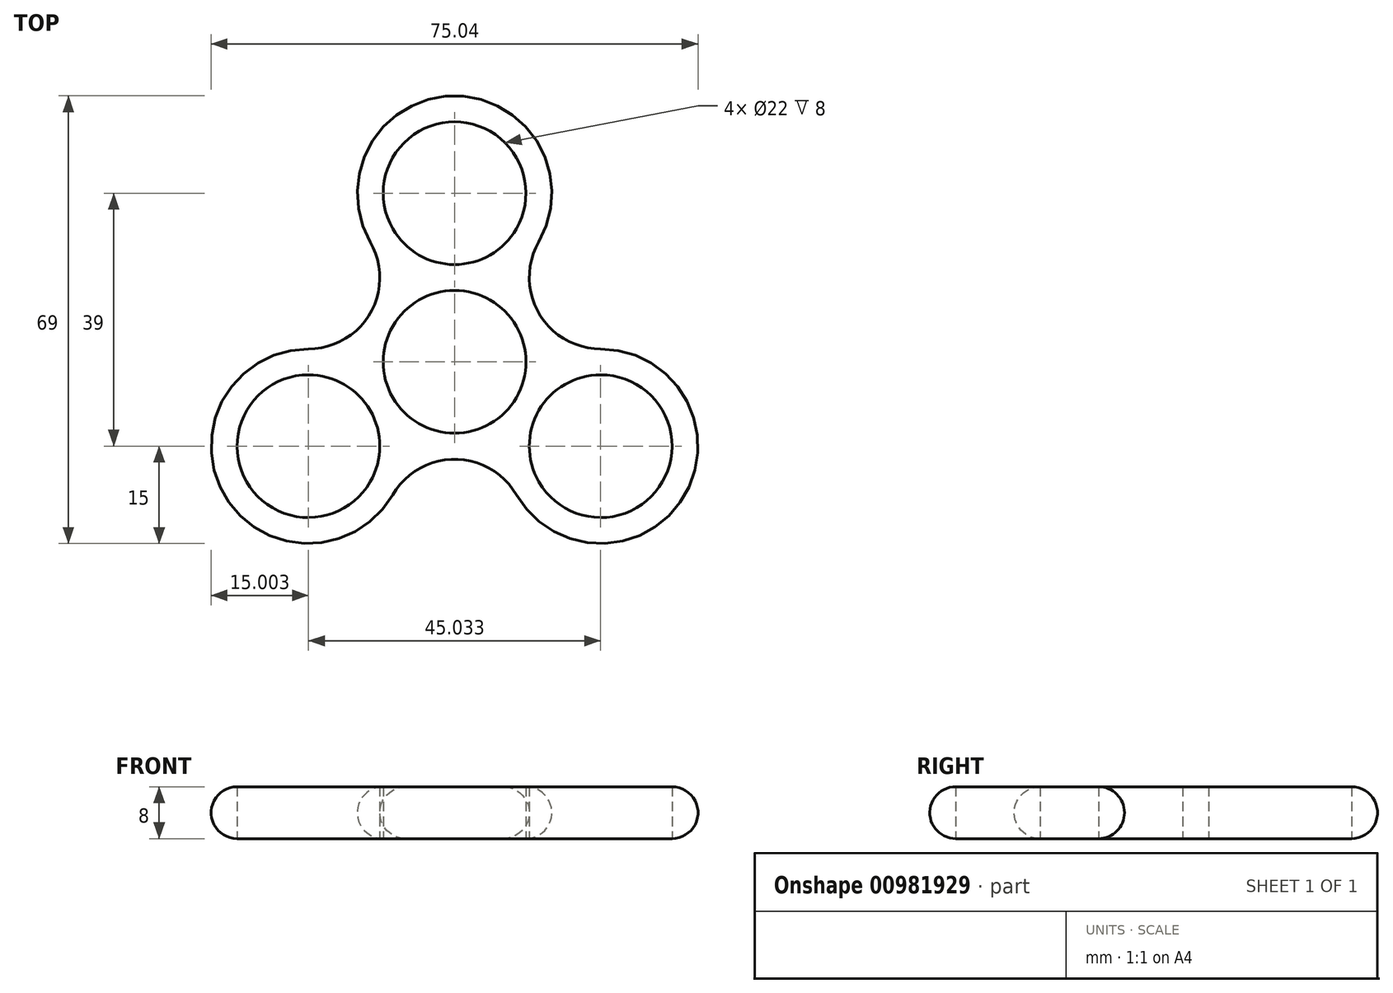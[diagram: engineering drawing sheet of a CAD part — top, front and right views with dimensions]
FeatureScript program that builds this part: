
annotation { "Feature Type Name" : "Feature", "Feature Type Description" : "" }
export const myFeature = defineFeature(function(context is Context, id is Id, definition is map)
    precondition{}
    {
        {
            var Q0;
            Q0=qCreatedBy(makeId("Top.planeOp"),FACE);
            var sketch = newSketch(context, id + "F0", { "sketchPlane" : qUnion([Q0])});
            skCircle(sketch, "E0", {"center": v(0, 0) * mm, "radius": 11 * mm});
            skCircle(sketch, "E1", {"center": v(0, 26) * mm, "radius": 11 * mm});
            skArc(sketch, "E2", {"start": v(13, 18.5) * mm, "mid": v(0, 41) * mm, "end": v(-13, 18.5) * mm});
            skArc(sketch, "E3.1.0", {"start": v(-22.52, 2) * mm, "mid": v(-35.5, -20.5) * mm, "end": v(-9.53, -20.5) * mm});
            skCircle(sketch, "E3.1.1", {"center": v(-22.52, -13) * mm, "radius": 11 * mm});
            skArc(sketch, "E3.2.0", {"start": v(15.02, 0) * mm, "mid": v(15, -0.01) * mm, "end": v(15, -0.02) * mm});
            skCircle(sketch, "E3.2.1", {"center": v(22.52, -13) * mm, "radius": 11 * mm});
            skArc(sketch, "E4", {"start": v(7.52, 12.98) * mm, "mid": v(7.5, 13) * mm, "end": v(7.48, 13) * mm});
            skLineSegment(sketch, "E5", {"start": v(7.52, -13) * mm, "end": v(7.48, -13) * mm, "construction": true});
            skArc(sketch, "E6", {"start": v(-22.52, 2) * mm, "mid": v(-13, 7.5) * mm, "end": v(-13, 18.5) * mm});
            skArc(sketch, "E7.1.0", {"start": v(9.53, -20.5) * mm, "mid": v(0, -15) * mm, "end": v(-9.53, -20.5) * mm});
            skArc(sketch, "E7.2.0", {"start": v(13, 18.5) * mm, "mid": v(13, 7.5) * mm, "end": v(22.52, 2) * mm});
            skLineSegment(sketch, "E8.trimOffspring", {"start": v(7.52, 12.98) * mm, "end": v(7.5, 13) * mm, "construction": true});
            skArc(sketch, "E9.trimOffspring", {"start": v(-7.48, 13) * mm, "mid": v(-7.5, 13) * mm, "end": v(-7.52, 12.98) * mm});
            skArc(sketch, "E10.trimOffspring", {"start": v(7.48, 13) * mm, "mid": v(7.5, 13) * mm, "end": v(7.5, 13) * mm});
            skArc(sketch, "E11.trimOffspring", {"start": v(-7.5, 13) * mm, "mid": v(-7.5, 13) * mm, "end": v(-7.48, 13) * mm});
            skArc(sketch, "E12.trimOffspring", {"start": v(-15, 0.02) * mm, "mid": v(-15, 0) * mm, "end": v(-15, -0.02) * mm});
            skLineSegment(sketch, "E13.trimOffspring", {"start": v(-7.52, 12.98) * mm, "end": v(-7.5, 13) * mm, "construction": true});
            skLineSegment(sketch, "E14.trimOffspring", {"start": v(-15.02, 0) * mm, "end": v(-15, 0.02) * mm, "construction": true});
            skArc(sketch, "E15.trimOffspring", {"start": v(-7.52, -12.98) * mm, "mid": v(-7.5, -13) * mm, "end": v(-7.48, -13) * mm});
            skArc(sketch, "E16.trimOffspring", {"start": v(-15, -0.02) * mm, "mid": v(-15, -0.01) * mm, "end": v(-15.02, 0) * mm});
            skArc(sketch, "E17.trimOffspring", {"start": v(7.52, -12.98) * mm, "mid": v(7.52, -13) * mm, "end": v(7.52, -13) * mm});
            skArc(sketch, "E18.trimOffspring", {"start": v(15, -0.02) * mm, "mid": v(15, 0) * mm, "end": v(15, 0.02) * mm});
            skLineSegment(sketch, "E19.trimOffspring", {"start": v(15.02, 0) * mm, "end": v(15, 0.02) * mm, "construction": true});
            skArc(sketch, "E20.trimOffspring", {"start": v(7.48, -13) * mm, "mid": v(7.5, -13) * mm, "end": v(7.52, -12.98) * mm});
            skArc(sketch, "E21.trimOffspring", {"start": v(9.53, -20.5) * mm, "mid": v(35.5, -20.5) * mm, "end": v(22.52, 2) * mm});
            skLineSegment(sketch, "E22.trimOffspring", {"start": v(-7.48, -13) * mm, "end": v(-7.52, -13) * mm, "construction": true});
            skArc(sketch, "E23.trimOffspring", {"start": v(-7.52, -13) * mm, "mid": v(-7.52, -13) * mm, "end": v(-7.52, -12.98) * mm});
            skSolve(sketch);
        }
        {
            var Q0;
            Q0=makeQuery(id+"F0.imprint","IMPRINT",FACE,{"disambiguationData":[TD([[makeQuery(id+"F0.imprint","IMPRINT",EDGE,{"derivedFrom":sQuery(id+"F0.wireOp",EDGE,"E0")}),-1.0]])]});
            extrude(context, id + "F1", {"entities" : qUnion([Q0]), "depth" : 8 * mm, "offsetDistance" : 25 * mm});
        }
        {
            var Q0;
            Q0=makeQuery(id+"F1.opExtrude","SWEPT_FACE",FACE,{"disambiguationData":[OSD([sQuery(id+"F0.wireOp",EDGE,"E21.trimOffspring")])]});
            var Q1;
            Q1=makeQuery(id+"F1.opExtrude","SWEPT_FACE",FACE,{"disambiguationData":[OSD([sQuery(id+"F0.wireOp",EDGE,"E7.2.0")])]});
            var Q2;
            Q2=makeQuery(id+"F1.opExtrude","SWEPT_FACE",FACE,{"disambiguationData":[OSD([sQuery(id+"F0.wireOp",EDGE,"E2")])]});
            var Q3;
            Q3=makeQuery(id+"F1.opExtrude","SWEPT_FACE",FACE,{"disambiguationData":[OSD([sQuery(id+"F0.wireOp",EDGE,"E6")])]});
            var Q4;
            Q4=makeQuery(id+"F1.opExtrude","SWEPT_FACE",FACE,{"disambiguationData":[OSD([sQuery(id+"F0.wireOp",EDGE,"E3.1.0")])]});
            var Q5;
            Q5=makeQuery(id+"F1.opExtrude","SWEPT_FACE",FACE,{"disambiguationData":[OSD([sQuery(id+"F0.wireOp",EDGE,"E7.1.0")])]});
            fillet(context, id + "F2", {"entities" : qUnion([Q0, Q1, Q2, Q3, Q4, Q5]), "radius" : 4 * mm, "tangentPropagation" : true, "allowEdgeOverflow" : false});
        }
    });
